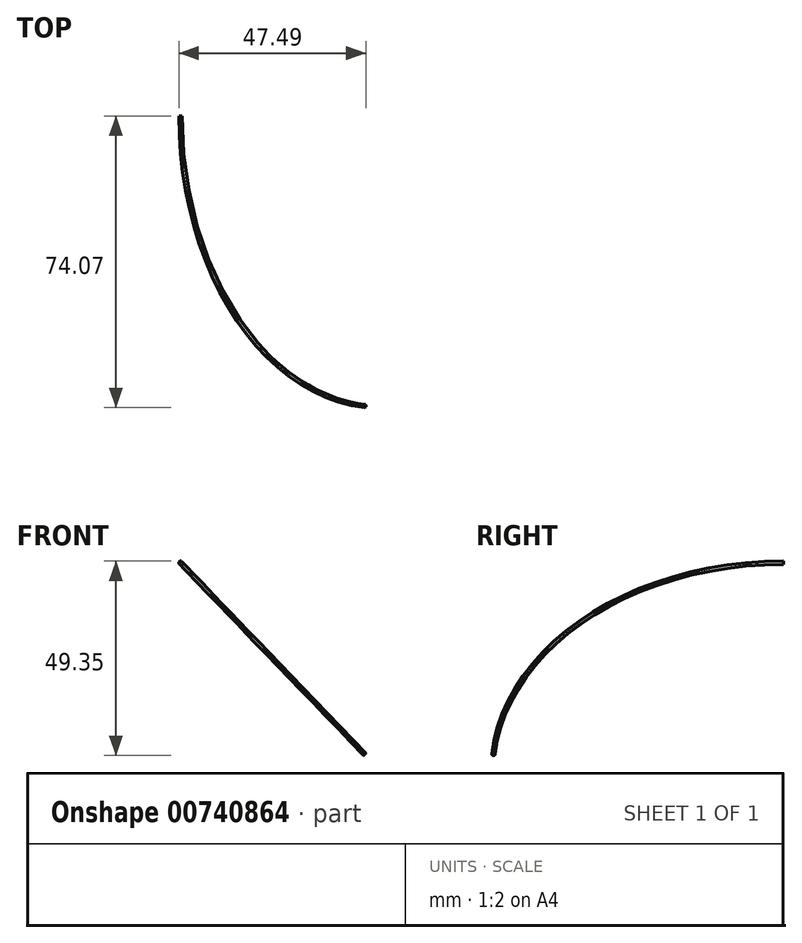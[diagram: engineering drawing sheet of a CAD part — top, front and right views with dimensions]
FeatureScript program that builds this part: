
annotation { "Feature Type Name" : "Feature", "Feature Type Description" : "" }
export const myFeature = defineFeature(function(context is Context, id is Id, definition is map)
    precondition{}
    {
        {
            var Q0;
            Q0=qCreatedBy(makeId("Front.planeOp"),FACE);
            var sketch = newSketch(context, id + "F0", { "sketchPlane" : qUnion([Q0])});
            skCircle(sketch, "E0", {"center": v(-75.69, 29.8) * mm, "radius": 0.4 * mm});
            skSolve(sketch);
        }
        {
            var Q0;
            Q0=qCreatedBy(makeId("Front.planeOp"),FACE);
            var sketch = newSketch(context, id + "F1", { "sketchPlane" : qUnion([Q0])});
            skLineSegment(sketch, "E1", {"start": v(0, 0) * mm, "end": v(8.99, 8.64) * mm});
            skSolve(sketch);
        }
        {
            var Q0;
            Q0=makeQuery(id+"F0.imprint","IMPRINT",FACE,{"disambiguationData":[TD([[makeQuery(id+"F0.imprint","IMPRINT",EDGE,{"derivedFrom":sQuery(id+"F0.wireOp",EDGE,"E0")}),1.0]])]});
            var Q1;
            Q1=sQuery(id+"F1.wireOp",EDGE,"E1");
            revolve(context, id + "F2", {"surfaceOperationType" : NewSurfaceOperationType.NEW, "entities" : qUnion([Q0]), "axis" : qUnion([Q1]), "revolveType" : RevolveType.ONE_DIRECTION, "angle" : 85 * degree});
        }
    });
